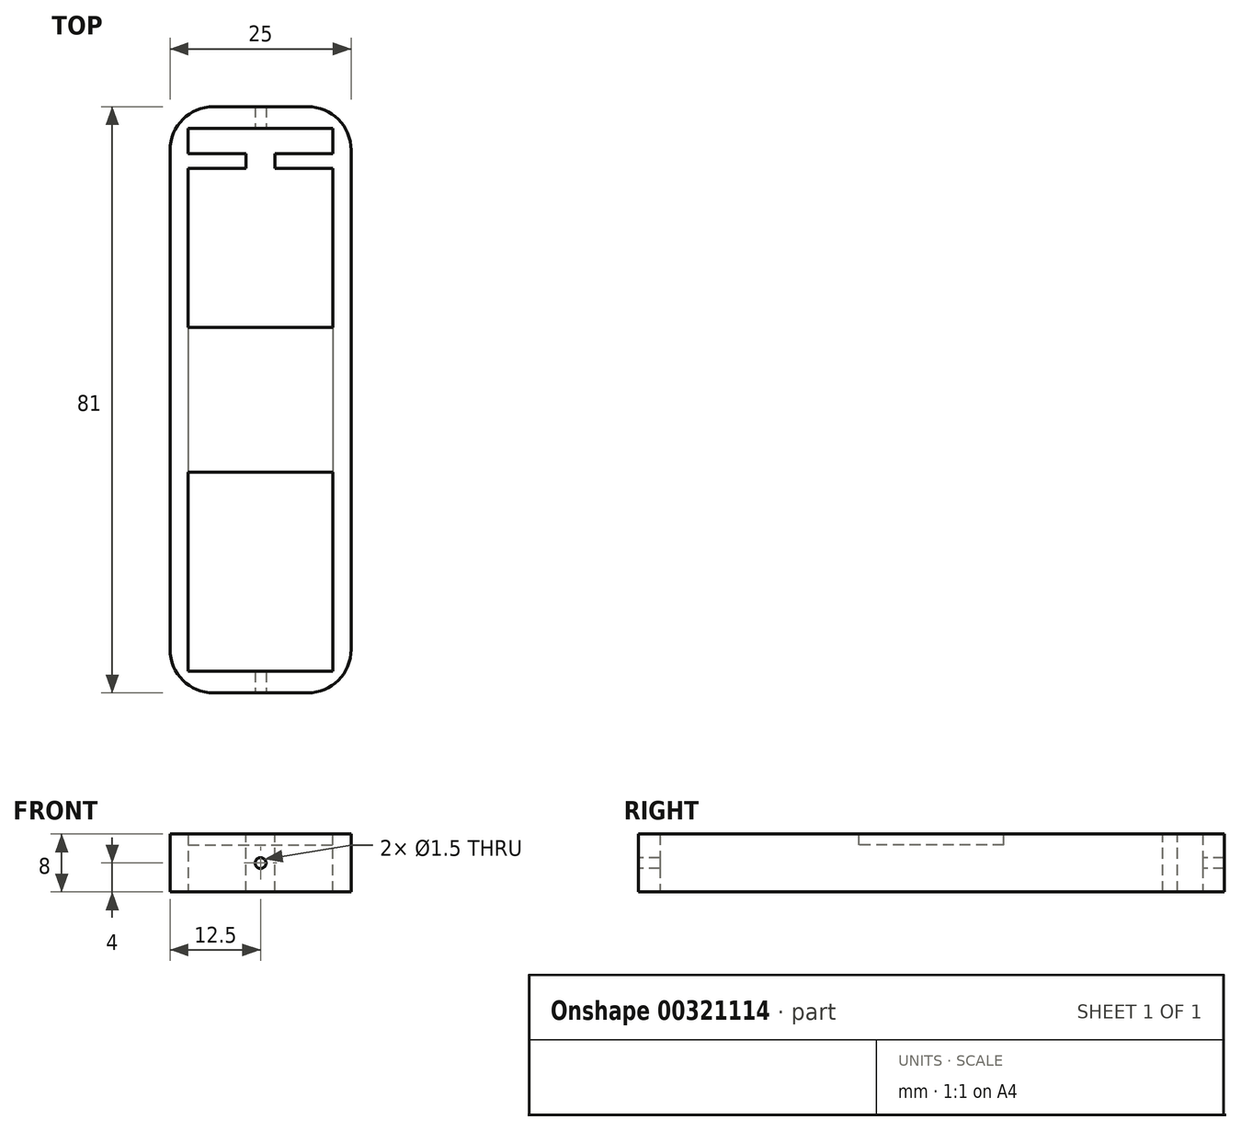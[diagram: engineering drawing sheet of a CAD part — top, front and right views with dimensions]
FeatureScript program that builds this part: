
annotation { "Feature Type Name" : "Feature", "Feature Type Description" : "" }
export const myFeature = defineFeature(function(context is Context, id is Id, definition is map)
    precondition{}
    {
        {
            var Q0;
            Q0=qCreatedBy(makeId("Top.planeOp"),FACE);
            var sketch = newSketch(context, id + "F0", { "sketchPlane" : qUnion([Q0])});
            skLineSegment(sketch, "E0.bottom", {"start": v(-10, 37.5) * mm, "end": v(10, 37.5) * mm});
            skLineSegment(sketch, "E0.top", {"start": v(-10, -37.5) * mm, "end": v(10, -37.5) * mm});
            skLineSegment(sketch, "E0.left", {"start": v(-10, 37.5) * mm, "end": v(-10, -37.5) * mm});
            skLineSegment(sketch, "E0.right", {"start": v(10, 37.5) * mm, "end": v(10, -37.5) * mm});
            skPoint(sketch, "E1", {"position": v(0, 37.5) * mm});
            skPoint(sketch, "E2", {"position": v(-10, 0) * mm});
            skLineSegment(sketch, "E3.bottom", {"start": v(-12.5, 40.5) * mm, "end": v(12.5, 40.5) * mm});
            skLineSegment(sketch, "E3.top", {"start": v(-12.5, -40.5) * mm, "end": v(12.5, -40.5) * mm});
            skLineSegment(sketch, "E3.left", {"start": v(-12.5, 40.5) * mm, "end": v(-12.5, -40.5) * mm});
            skLineSegment(sketch, "E3.right", {"start": v(12.5, 40.5) * mm, "end": v(12.5, -40.5) * mm});
            skPoint(sketch, "E4", {"position": v(-12.5, 0) * mm});
            skPoint(sketch, "E5", {"position": v(0, 40.5) * mm});
            skSolve(sketch);
        }
        {
            var Q0;
            Q0 = qSketchRegion(id + "F0", true);
            extrude(context, id + "F1", {"entities" : qUnion([Q0]), "depth" : 8 * mm});
        }
        {
            var Q0;
            Q0=makeQuery(id+"F1.opExtrude","CAP_FACE",FACE,{"disambiguationData":[OSD([sQuery(id+"F0.wireOp",EDGE,"E0.bottom"),sQuery(id+"F0.wireOp",EDGE,"E0.top"),sQuery(id+"F0.wireOp",EDGE,"E0.left"),sQuery(id+"F0.wireOp",EDGE,"E0.right"),sQuery(id+"F0.wireOp",EDGE,"E3.bottom"),sQuery(id+"F0.wireOp",EDGE,"E3.top"),sQuery(id+"F0.wireOp",EDGE,"E3.left"),sQuery(id+"F0.wireOp",EDGE,"E3.right")])],"isStart":false});
            var sketch = newSketch(context, id + "F2", { "sketchPlane" : qUnion([Q0])});
            skLineSegment(sketch, "E6.bottom", {"start": v(-10, 34) * mm, "end": v(-2, 34) * mm});
            skLineSegment(sketch, "E6.top", {"start": v(-10, 32) * mm, "end": v(-2, 32) * mm});
            skLineSegment(sketch, "E6.left", {"start": v(-10, 34) * mm, "end": v(-10, 32) * mm});
            skLineSegment(sketch, "E6.right", {"start": v(-2, 34) * mm, "end": v(-2, 32) * mm});
            skLineSegment(sketch, "E7.MirrorCS", {"start": v(10, 34) * mm, "end": v(2, 34) * mm});
            skLineSegment(sketch, "E8.MirrorCS", {"start": v(10, 32) * mm, "end": v(2, 32) * mm});
            skLineSegment(sketch, "E9.MirrorCS", {"start": v(10, 34) * mm, "end": v(10, 32) * mm});
            skLineSegment(sketch, "E10.MirrorCS", {"start": v(2, 34) * mm, "end": v(2, 32) * mm});
            skSolve(sketch);
        }
        {
            var Q0;
            Q0 = qSketchRegion(id + "F2", true);
            extrude(context, id + "F3", {"entities" : qUnion([Q0]), "operationType" : NewBodyOperationType.ADD, "oppositeDirection" : true, "depth" : 8 * mm});
        }
        {
            var Q0;
            Q0=makeQuery(id+"F3.boolean.opBoolean","MERGE",FACE,{"derivedFrom":[makeQuery(id+"F1.opExtrude","CAP_FACE",FACE,{"disambiguationData":[OSD([sQuery(id+"F0.wireOp",EDGE,"E0.bottom"),sQuery(id+"F0.wireOp",EDGE,"E0.top"),sQuery(id+"F0.wireOp",EDGE,"E0.left"),sQuery(id+"F0.wireOp",EDGE,"E0.right"),sQuery(id+"F0.wireOp",EDGE,"E3.bottom"),sQuery(id+"F0.wireOp",EDGE,"E3.top"),sQuery(id+"F0.wireOp",EDGE,"E3.left"),sQuery(id+"F0.wireOp",EDGE,"E3.right")])],"isStart":false}),makeQuery(id+"F3.opExtrude","CAP_FACE",FACE,{"disambiguationData":[OSD([sQuery(id+"F2.wireOp",EDGE,"E6.bottom"),sQuery(id+"F2.wireOp",EDGE,"E6.top"),sQuery(id+"F2.wireOp",EDGE,"E6.left"),sQuery(id+"F2.wireOp",EDGE,"E6.right")])],"isStart":true}),makeQuery(id+"F3.opExtrude","CAP_FACE",FACE,{"disambiguationData":[OSD([sQuery(id+"F2.wireOp",EDGE,"E7.MirrorCS"),sQuery(id+"F2.wireOp",EDGE,"E8.MirrorCS"),sQuery(id+"F2.wireOp",EDGE,"E9.MirrorCS"),sQuery(id+"F2.wireOp",EDGE,"E10.MirrorCS")])],"isStart":true})]});
            var sketch = newSketch(context, id + "F4", { "sketchPlane" : qUnion([Q0])});
            skPoint(sketch, "E11", {"position": v(-2, 32) * mm});
            skSolve(sketch);
        }
        {
            var Q0;
            Q0=makeQuery(id+"F1.opExtrude","SWEPT_EDGE",EDGE,{"disambiguationData":[OSD([sQuery(id+"F0.wireOp",EDGE,"E3.bottom"),sQuery(id+"F0.wireOp",EDGE,"E3.left")])]});
            var Q1;
            Q1=makeQuery(id+"F1.opExtrude","SWEPT_EDGE",EDGE,{"disambiguationData":[OSD([sQuery(id+"F0.wireOp",EDGE,"E3.bottom"),sQuery(id+"F0.wireOp",EDGE,"E3.right")])]});
            var Q2;
            Q2=makeQuery(id+"F1.opExtrude","SWEPT_EDGE",EDGE,{"disambiguationData":[OSD([sQuery(id+"F0.wireOp",EDGE,"E3.top"),sQuery(id+"F0.wireOp",EDGE,"E3.right")])]});
            var Q3;
            Q3=makeQuery(id+"F1.opExtrude","SWEPT_EDGE",EDGE,{"disambiguationData":[OSD([sQuery(id+"F0.wireOp",EDGE,"E3.top"),sQuery(id+"F0.wireOp",EDGE,"E3.left")])]});
            fillet(context, id + "F5", {"entities" : qUnion([Q0, Q1, Q2, Q3]), "radius" : 6 * mm, "tangentPropagation" : true, "allowEdgeOverflow" : false});
        }
        {
            var Q0;
            {var subQ6=sQuery(id+"F0.wireOp",EDGE,"E0.bottom");Q0=makeQuery(id+"F4.imprint","IMPRINT",FACE,{"disambiguationData":[TD([[makeQuery(id+"F4.imprint","IMPRINT",EDGE,{"derivedFrom":makeQuery(id+"F1.opExtrude","CAP_EDGE",EDGE,{"disambiguationData":[OSD([subQ6])],"isStart":false})}),1.0]])]});}
            var sketch = newSketch(context, id + "F6", { "sketchPlane" : qUnion([Q0])});
            skLineSegment(sketch, "E12.bottom", {"start": v(-12.5, 10) * mm, "end": v(10, 10) * mm});
            skLineSegment(sketch, "E12.top", {"start": v(-12.5, -10) * mm, "end": v(10, -10) * mm});
            skLineSegment(sketch, "E12.left", {"start": v(-12.5, 10) * mm, "end": v(-12.5, -10) * mm});
            skLineSegment(sketch, "E12.right", {"start": v(10, 10) * mm, "end": v(10, -10) * mm});
            skPoint(sketch, "E13", {"position": v(-12.5, 0) * mm});
            skSolve(sketch);
        }
        {
            var Q0;
            Q0 = qSketchRegion(id + "F6", true);
            extrude(context, id + "F7", {"entities" : qUnion([Q0]), "operationType" : NewBodyOperationType.ADD, "oppositeDirection" : true, "depth" : 1.5 * mm});
        }
        {
            var Q0;
            Q0=makeQuery(id+"F1.opExtrude","SWEPT_FACE",FACE,{"disambiguationData":[OSD([sQuery(id+"F0.wireOp",EDGE,"E3.top")])]});
            var sketch = newSketch(context, id + "F8", { "sketchPlane" : qUnion([Q0])});
            skCircle(sketch, "E14", {"center": v(0, 4) * mm, "radius": 0.75 * mm});
            skPoint(sketch, "E14.centerSnap0", {"position": v(0, 8) * mm});
            skPoint(sketch, "E15", {"position": v(-6.5, 4) * mm});
            skSolve(sketch);
        }
        {
            var Q0;
            Q0 = qSketchRegion(id + "F8", true);
            extrude(context, id + "F9", {"entities" : qUnion([Q0]), "operationType" : NewBodyOperationType.REMOVE, "oppositeDirection" : true, "depth" : 100 * mm});
        }
    });
